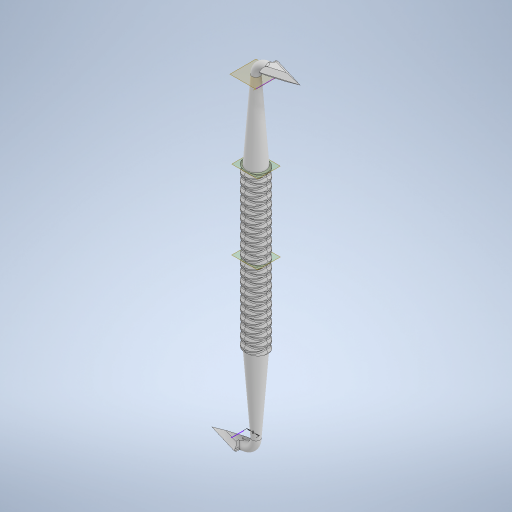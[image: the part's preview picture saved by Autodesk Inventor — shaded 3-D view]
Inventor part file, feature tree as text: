
AUTODESK INVENTOR PART (.ipt)
format: ipt  version: 2024 (Build 280153000, 153)  size: 2,764,800 bytes
history: native  units: mm
features: sketch x15, chamfer x12, extrude x7, helix x4, plane x3, revolve x2, fillet x2, other x1
ambient origin geometry x8: Origin, YZ Plane, XZ Plane, XY Plane, X Axis, Y Axis, Z Axis, Center Point
bodies: Solid1 (feature_tree)
feature tree (46):
  extrude  "Extrusion1"  Depth=2.0mm TaperAngle=0.0deg
  helix  "Coil1"  [1 undecoded]
  helix  "Coil2"  [1 undecoded]
  helix  "Coil3"  [1 undecoded]
  helix  "Coil4"  [1 undecoded]
  chamfer  "Chamfer1"  Distance=2.0mm Angle=45.0deg
  chamfer  "Chamfer2"  Distance=2.0mm Angle=45.0deg
  chamfer  "Chamfer3"  Distance=2.0mm Angle=45.0deg
  chamfer  "Chamfer4"  Distance=2.0mm Angle=45.0deg
  chamfer  "Chamfer5"  Distance=2.0mm Angle=45.0deg
  chamfer  "Chamfer6"  Distance=2.0mm Angle=45.0deg
  chamfer  "Chamfer7"  Distance=2.0mm Angle=45.0deg
  chamfer  "Chamfer8"  Distance=50.0mm
  extrude  "Extrusion2"  TaperAngle=90.0deg  [1 undecoded]
  chamfer  "Chamfer9"  Distance=50.0mm
  sketch  "Sketch9"  dims[d65=50.0mm d66=50.0mm d67=0.698132mm d68=90.0deg]
  plane  "Work Plane3"
  sketch  "Sketch10"  dims[d69=-50.0mm]
  other  "Work Axis2"
  revolve  "Revolution1"  [1 undecoded]
  plane  "Work Plane4"
  plane  "Work Plane5"
  extrude  "Extrusion3"  Depth=12.0mm
  chamfer  "Chamfer10"  Distance=20.0mm
  sketch  "Sketch12"  dims[d71=12.0mm d72=50.0mm d73=0.0mm]
  revolve  "Revolution2"  Angle=45.0deg
  extrude  "Extrusion4"  Depth=2.0mm
  extrude  "Extrusion5"  Depth=2.0mm TaperAngle=0.0deg
  chamfer  "Chamfer11"  Distance=20.0mm
  extrude  "Extrusion6"  Depth=2.0mm TaperAngle=45.0deg
  extrude  "Extrusion7"  Depth=2.0mm
  chamfer  "Chamfer12"  Distance=2.0mm
  fillet  "Fillet1"  [1 undecoded]
  fillet  "Fillet2"  [1 undecoded]
  sketch  "Sketch1"  dims[d0=15.0mm d1=100.0mm d2=0.0mm d3=2.0mm]
  sketch  "Sketch2"  dims[d4=10.0mm d5=10.0mm d6=100.0mm d7=0.0mm d8=90.0deg d9=90.0deg d10=0.0mm d11=0.0mm]
  sketch  "Sketch4"  dims[d12=10.0mm d13=10.0mm d14=100.0mm d15=0.0mm d16=90.0deg d17=90.0deg d18=0.0mm d19=0.0mm d20=2.0mm]
  sketch  "Sketch5"  dims[d21=10.0mm d22=10.0mm d23=100.0mm d24=0.0mm d25=90.0deg d26=90.0deg d27=0.0mm d28=0.0mm d29=2.0mm]
  sketch  "Sketch6"  dims[d30=10.0mm d31=10.0mm d32=100.0mm d33=0.0mm d34=90.0deg d35=90.0deg d36=0.0mm d37=0.0mm d38=1.0mm d39=2.0mm d40=45.0deg d41=1.0mm d42=2.0mm d43=45.0deg d44=1.0mm d45=2.0mm d46=45.0deg d47=1.0mm d48=2.0mm d49=45.0deg d50=1.0mm d51=2.0mm d52=45.0deg d53=1.0mm d54=2.0mm d55=45.0deg d56=1.0mm d57=2.0mm d58=45.0deg d59=1.0mm d60=2.0mm d61=45.0deg]
  sketch  "Sketch8"  dims[d62=12.0mm d63=50.0mm d64=0.0mm]
  sketch  "Sketch11"  dims[d70=-100.0mm]
  sketch  "Sketch13"  dims[d74=50.0mm d75=50.0mm d76=0.698132mm d77=8.0mm]
  sketch  "Sketch14"  dims[d78=90.0deg d79=12.0mm]
  sketch  "Sketch15"  dims[d80=5.007mm d81=20.0mm d82=0.0mm]
  sketch  "Sketch16"  dims[d83=20.0mm d84=0.0mm d85=2.5mm d86=2.0mm d87=45.0deg]
  sketch  "Sketch17"  dims[d88=12.0mm d89=5.007mm d90=20.0mm d91=0.0mm d92=20.0mm d93=0.0mm d94=2.5mm d95=2.0mm d96=45.0deg d97=2.0mm d98=2.0mm]
note: 8 required parameter values undecoded (feature->parameter linkage not recoverable at this tier; creation-order binding heuristic only, values carry confidence <= 0.55)